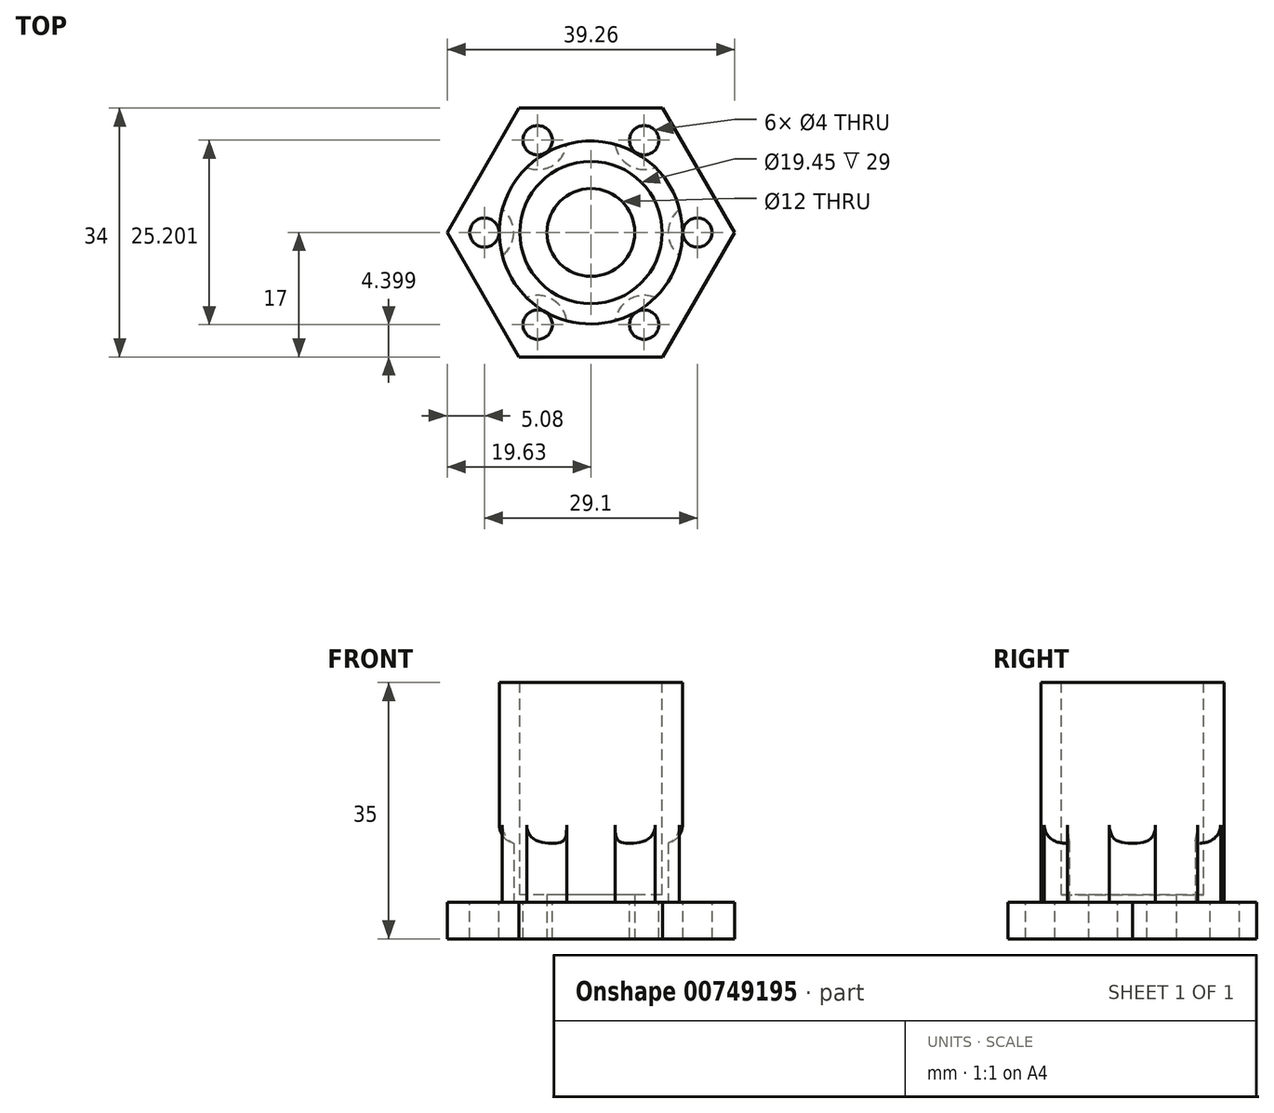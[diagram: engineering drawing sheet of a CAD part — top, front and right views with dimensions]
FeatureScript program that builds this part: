
annotation { "Feature Type Name" : "Feature", "Feature Type Description" : "" }
export const myFeature = defineFeature(function(context is Context, id is Id, definition is map)
    precondition{}
    {
        {
            var Q0;
            Q0=qCreatedBy(makeId("Top.planeOp"),FACE);
            var sketch = newSketch(context, id + "F0", { "sketchPlane" : qUnion([Q0])});
            skCircle(sketch, "E0.cCircle", {"center": v(0, 0) * mm, "radius": 17 * mm, "construction": true});
            skLineSegment(sketch, "E0.0", {"start": v(-9.81, 17) * mm, "end": v(9.81, 17) * mm});
            skLineSegment(sketch, "E0.1", {"start": v(9.81, 17) * mm, "end": v(19.63, 0) * mm});
            skLineSegment(sketch, "E0.2", {"start": v(19.63, 0) * mm, "end": v(9.81, -17) * mm});
            skLineSegment(sketch, "E0.3", {"start": v(9.81, -17) * mm, "end": v(-9.81, -17) * mm});
            skLineSegment(sketch, "E0.4", {"start": v(-9.81, -17) * mm, "end": v(-19.63, 0) * mm});
            skLineSegment(sketch, "E0.5", {"start": v(-19.63, 0) * mm, "end": v(-9.81, 17) * mm});
            skPoint(sketch, "E0.0.midPoint", {"position": v(0, 17) * mm});
            skSolve(sketch);
        }
        {
            var Q0;
            Q0=qSketchRegion(id+"F0",true);
            extrude(context, id + "F1", {"entities" : qUnion([Q0]), "depth" : 5 * mm, "offsetDistance" : 25.4 * mm});
        }
        {
            var Q0;
            Q0=makeQuery(id+"F1.opExtrude","CAP_FACE",FACE,{"disambiguationData":[OSD([sQuery(id+"F0.wireOp",EDGE,"E0.0"),sQuery(id+"F0.wireOp",EDGE,"E0.1"),sQuery(id+"F0.wireOp",EDGE,"E0.2"),sQuery(id+"F0.wireOp",EDGE,"E0.3"),sQuery(id+"F0.wireOp",EDGE,"E0.4"),sQuery(id+"F0.wireOp",EDGE,"E0.5")])],"isStart":false});
            var sketch = newSketch(context, id + "F2", { "sketchPlane" : qUnion([Q0])});
            skCircle(sketch, "E1", {"center": v(0, 0) * mm, "radius": 12.5 * mm});
            skSolve(sketch);
        }
        {
            var Q0;
            Q0=qSketchRegion(id+"F2",true);
            extrude(context, id + "F3", {"entities" : qUnion([Q0]), "operationType" : NewBodyOperationType.ADD, "depth" : 30 * mm, "offsetDistance" : 25.4 * mm});
        }
        {
            var Q0;
            Q0=makeQuery(id+"F3.opExtrude","CAP_FACE",FACE,{"disambiguationData":[OSD([sQuery(id+"F2.wireOp",EDGE,"E1")])],"isStart":false});
            var sketch = newSketch(context, id + "F4", { "sketchPlane" : qUnion([Q0])});
            skCircle(sketch, "E2", {"center": v(0, 0) * mm, "radius": 9.72 * mm});
            skSolve(sketch);
        }
        {
            var Q0;
            Q0=qSketchRegion(id+"F4",true);
            extrude(context, id + "F5", {"entities" : qUnion([Q0]), "operationType" : NewBodyOperationType.REMOVE, "oppositeDirection" : true, "depth" : 29 * mm, "offsetDistance" : 25.4 * mm});
        }
        {
            var Q0;
            Q0=makeQuery(id+"F1.opExtrude","CAP_FACE",FACE,{"disambiguationData":[OSD([sQuery(id+"F0.wireOp",EDGE,"E0.0"),sQuery(id+"F0.wireOp",EDGE,"E0.1"),sQuery(id+"F0.wireOp",EDGE,"E0.2"),sQuery(id+"F0.wireOp",EDGE,"E0.3"),sQuery(id+"F0.wireOp",EDGE,"E0.4"),sQuery(id+"F0.wireOp",EDGE,"E0.5")])],"isStart":true});
            var sketch = newSketch(context, id + "F6", { "sketchPlane" : qUnion([Q0])});
            skCircle(sketch, "E3", {"center": v(0, 0) * mm, "radius": 6 * mm});
            skSolve(sketch);
        }
        {
            var Q0;
            Q0=qSketchRegion(id+"F6",true);
            extrude(context, id + "F7", {"entities" : qUnion([Q0]), "operationType" : NewBodyOperationType.REMOVE, "oppositeDirection" : true, "depth" : 25.4 * mm, "offsetDistance" : 25.4 * mm});
        }
        {
            var Q0;
            Q0=makeQuery(id+"F1.opExtrude","CAP_FACE",FACE,{"disambiguationData":[OSD([sQuery(id+"F0.wireOp",EDGE,"E0.0"),sQuery(id+"F0.wireOp",EDGE,"E0.1"),sQuery(id+"F0.wireOp",EDGE,"E0.2"),sQuery(id+"F0.wireOp",EDGE,"E0.3"),sQuery(id+"F0.wireOp",EDGE,"E0.4"),sQuery(id+"F0.wireOp",EDGE,"E0.5")])],"isStart":false});
            var sketch = newSketch(context, id + "F8", { "sketchPlane" : qUnion([Q0])});
            skCircle(sketch, "E4", {"center": v(-7.27, 12.6) * mm, "radius": 2 * mm});
            skLineSegment(sketch, "E5", {"start": v(-9.81, 17) * mm, "end": v(9.81, -17) * mm});
            skLineSegment(sketch, "E6", {"start": v(9.81, 17) * mm, "end": v(-9.81, -17) * mm});
            skLineSegment(sketch, "E7", {"start": v(19.63, 0) * mm, "end": v(-19.63, 0) * mm});
            skCircle(sketch, "E8", {"center": v(14.55, 0) * mm, "radius": 2 * mm});
            skCircle(sketch, "E9", {"center": v(7.27, 12.6) * mm, "radius": 2 * mm});
            skCircle(sketch, "E10", {"center": v(-14.55, 0) * mm, "radius": 2 * mm});
            skCircle(sketch, "E11", {"center": v(-7.27, -12.6) * mm, "radius": 2 * mm});
            skCircle(sketch, "E12", {"center": v(7.27, -12.6) * mm, "radius": 2 * mm});
            skSolve(sketch);
        }
        {
            var Q0;
            Q0=qSketchRegion(id+"F8",true);
            extrude(context, id + "F9", {"entities" : qUnion([Q0]), "operationType" : NewBodyOperationType.REMOVE, "oppositeDirection" : true, "depth" : 25.4 * mm, "offsetDistance" : 25.4 * mm});
        }
        {
            var Q0;
            Q0=makeQuery(id+"F1.opExtrude","CAP_FACE",FACE,{"disambiguationData":[OSD([sQuery(id+"F0.wireOp",EDGE,"E0.0"),sQuery(id+"F0.wireOp",EDGE,"E0.1"),sQuery(id+"F0.wireOp",EDGE,"E0.2"),sQuery(id+"F0.wireOp",EDGE,"E0.3"),sQuery(id+"F0.wireOp",EDGE,"E0.4"),sQuery(id+"F0.wireOp",EDGE,"E0.5")])],"isStart":false});
            var sketch = newSketch(context, id + "F10", { "sketchPlane" : qUnion([Q0])});
            skCircle(sketch, "E13", {"center": v(-7.27, -12.6) * mm, "radius": 4 * mm});
            skCircle(sketch, "E14", {"center": v(-14.55, 0) * mm, "radius": 4 * mm});
            skCircle(sketch, "E15", {"center": v(-7.27, 12.6) * mm, "radius": 4 * mm});
            skCircle(sketch, "E16", {"center": v(7.27, 12.6) * mm, "radius": 4 * mm});
            skCircle(sketch, "E17", {"center": v(14.55, 0) * mm, "radius": 4 * mm});
            skCircle(sketch, "E18", {"center": v(7.27, -12.6) * mm, "radius": 4 * mm});
            skSolve(sketch);
        }
        {
            var Q0;
            Q0=qSketchRegion(id+"F10",true);
            extrude(context, id + "F11", {"entities" : qUnion([Q0]), "operationType" : NewBodyOperationType.REMOVE, "depth" : 8 * mm, "offsetDistance" : 25.4 * mm});
        }
        {
            var Q0;
            Q0=makeQuery(id+"F11.boolean.opBoolean","INTERSECT",EDGE,{"derivedFrom":[makeQuery(id+"F3.opExtrude","SWEPT_FACE",FACE,{"disambiguationData":[OSD([sQuery(id+"F2.wireOp",EDGE,"E1")])]}),makeQuery(id+"F11.opExtrude","CAP_FACE",FACE,{"disambiguationData":[OSD([sQuery(id+"F10.wireOp",EDGE,"E14")])],"isStart":false})]});
            var Q1;
            Q1=makeQuery(id+"F11.boolean.opBoolean","INTERSECT",EDGE,{"derivedFrom":[makeQuery(id+"F3.opExtrude","SWEPT_FACE",FACE,{"disambiguationData":[OSD([sQuery(id+"F2.wireOp",EDGE,"E1")])]}),makeQuery(id+"F11.opExtrude","CAP_FACE",FACE,{"disambiguationData":[OSD([sQuery(id+"F10.wireOp",EDGE,"E13")])],"isStart":false})]});
            var Q2;
            Q2=makeQuery(id+"F11.boolean.opBoolean","INTERSECT",EDGE,{"derivedFrom":[makeQuery(id+"F3.opExtrude","SWEPT_FACE",FACE,{"disambiguationData":[OSD([sQuery(id+"F2.wireOp",EDGE,"E1")])]}),makeQuery(id+"F11.opExtrude","CAP_FACE",FACE,{"disambiguationData":[OSD([sQuery(id+"F10.wireOp",EDGE,"E18")])],"isStart":false})]});
            var Q3;
            Q3=makeQuery(id+"F11.boolean.opBoolean","INTERSECT",EDGE,{"derivedFrom":[makeQuery(id+"F3.opExtrude","SWEPT_FACE",FACE,{"disambiguationData":[OSD([sQuery(id+"F2.wireOp",EDGE,"E1")])]}),makeQuery(id+"F11.opExtrude","CAP_FACE",FACE,{"disambiguationData":[OSD([sQuery(id+"F10.wireOp",EDGE,"E17")])],"isStart":false})]});
            var Q4;
            Q4=makeQuery(id+"F11.boolean.opBoolean","INTERSECT",EDGE,{"derivedFrom":[makeQuery(id+"F3.opExtrude","SWEPT_FACE",FACE,{"disambiguationData":[OSD([sQuery(id+"F2.wireOp",EDGE,"E1")])]}),makeQuery(id+"F11.opExtrude","CAP_FACE",FACE,{"disambiguationData":[OSD([sQuery(id+"F10.wireOp",EDGE,"E16")])],"isStart":false})]});
            var Q5;
            Q5=makeQuery(id+"F11.boolean.opBoolean","INTERSECT",EDGE,{"derivedFrom":[makeQuery(id+"F3.opExtrude","SWEPT_FACE",FACE,{"disambiguationData":[OSD([sQuery(id+"F2.wireOp",EDGE,"E1")])]}),makeQuery(id+"F11.opExtrude","CAP_FACE",FACE,{"disambiguationData":[OSD([sQuery(id+"F10.wireOp",EDGE,"E15")])],"isStart":false})]});
            fillet(context, id + "F12", {"entities" : qUnion([Q0, Q1, Q2, Q3, Q4, Q5]), "radius" : 2.54 * mm, "tangentPropagation" : true, "allowEdgeOverflow" : false});
        }
    });
